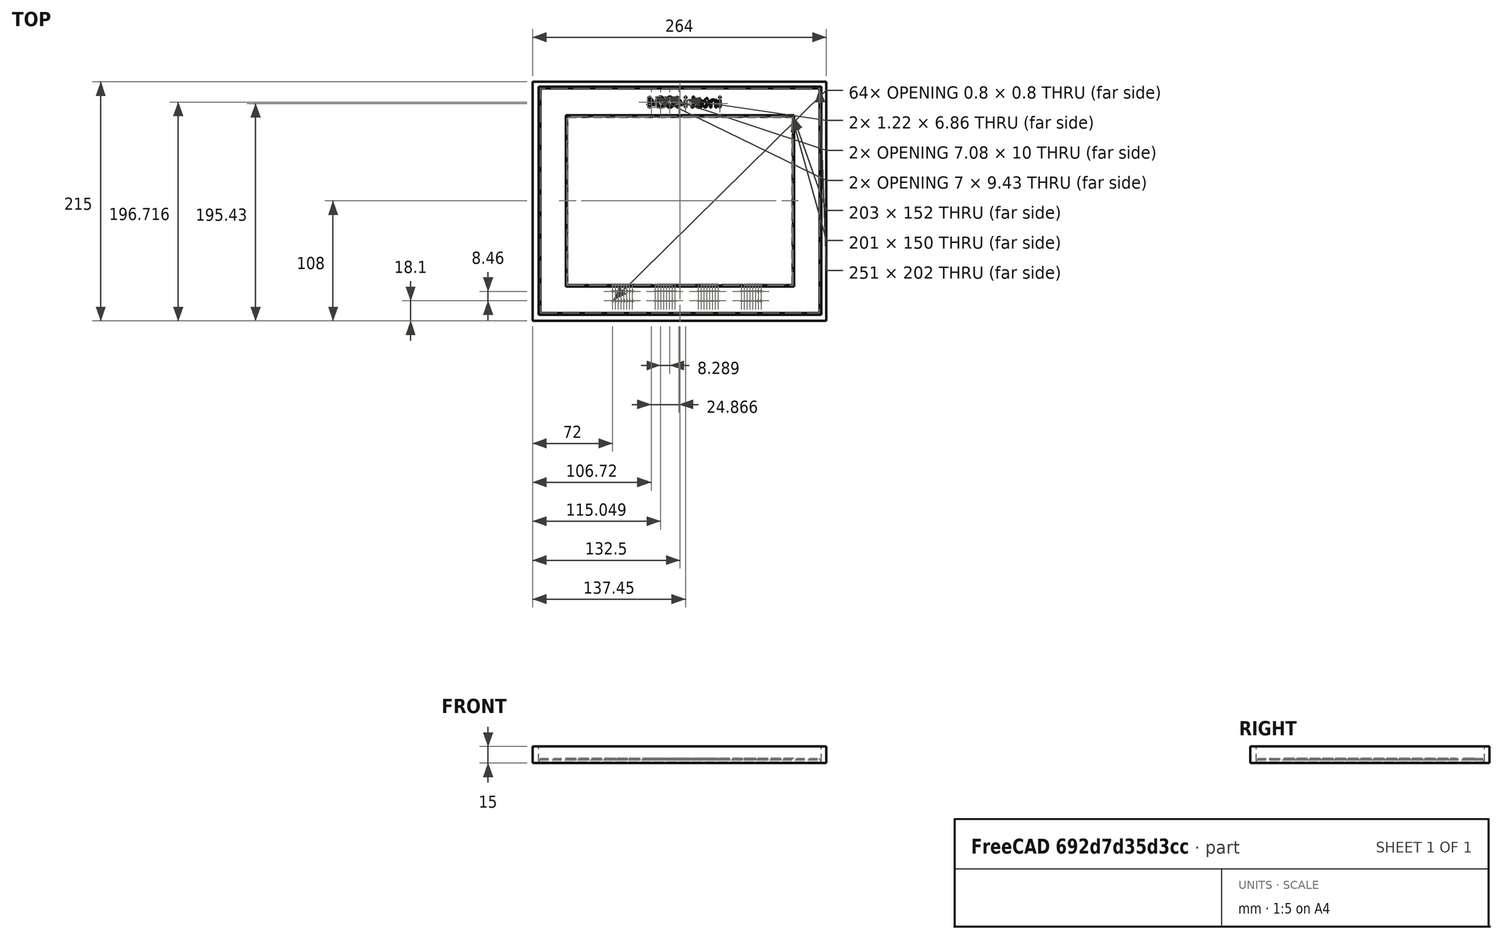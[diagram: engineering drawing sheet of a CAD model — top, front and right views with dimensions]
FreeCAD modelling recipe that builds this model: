
FCSTD DOCUMENT  (FreeCAD 0.18R4 (GitTag))
Label: Frame
License: All rights reserved
LicenseURL: http://en.wikipedia.org/wiki/All_rights_reserved
objects: Part::Box×9, Part::Cut×5, Part::Feature×5, Part::MultiFuse×2, App::DocumentObjectGroup×1, Part::Part2DObjectPython×1, Part::Extrusion×1
note: 23 computed .brp shape members not serialized (recipe doc carries the construction recipe); baked Part::Feature solids carry a one-line shape summary decoded from their .brp

FEATURE [Part::Box] Box  label="Picture"
  AttacherType = Attacher::AttachEngine3D
  Height = 0.1
  Length = 203
  Placement = pos=(31,32,4.14) rot=(0,0,1;0rad)
  Width = 152
FEATURE [Part::Box] Box002  label="Glass"
  AttacherType = Attacher::AttachEngine3D
  Height = 2.12
  Length = 253
  Placement = pos=(6,6,1) rot=(0,0,1;0rad)
  Width = 204
FEATURE [Part::Box] Box003  label="FrameOuter"
  AttacherType = Attacher::AttachEngine3D
  Height = 15
  Length = 264
  Width = 215
FEATURE [Part::Box] Box004  label="FrameCutOut1"
  AttacherType = Attacher::AttachEngine3D
  Height = 16
  Length = 254
  Placement = pos=(5.5,5.5,1) rot=(0,0,1;0rad)
  Width = 205
FEATURE [Part::Box] Box005  label="FrameCutOut2"
  AttacherType = Attacher::AttachEngine3D
  Height = 1
  Length = 251
  Placement = pos=(7,7,0) rot=(0,0,1;0rad)
  Width = 202
FEATURE [Part::Cut] Cut
  Base = -> Box003
  Tool = -> Box004
FEATURE [Part::Cut] Cut001  label="Frame (Model)"
  Base = -> Cut
  Tool = -> Box005
FEATURE [App::DocumentObjectGroup] Group  label="Frame001"
  Group = -> [Cut001,Box002]
FEATURE [Part::Box] Box007  label="InsertMain"
  AttacherType = Attacher::AttachEngine3D
  Height = 1
  Length = 251
  Placement = pos=(7,7,0) rot=(0,0,1;0rad)
  Width = 202
FEATURE [Part::Box] Box008  label="InsertCutOut"
  AttacherType = Attacher::AttachEngine3D
  Height = 1
  Length = 201
  Placement = pos=(32,33,0) rot=(0,0,1;0rad)
  Width = 150
FEATURE [Part::Cut] Cut002  label="Insert001"
  Base = -> Box007
  Placement = pos=(0,0,3.13) rot=(0,0,1;0rad)
  Tool = -> Box008
FEATURE [Part::Box] Box009  label="InsertGuideCutout"
  AttacherType = Attacher::AttachEngine3D
  Height = 0.5
  Length = 203
  Placement = pos=(31,32,4.14) rot=(0,0,1;0rad)
  Width = 152
FEATURE [Part::Box] Box010  label="InsertGuideMain"
  AttacherType = Attacher::AttachEngine3D
  Height = 0.5
  Length = 205
  Placement = pos=(30,31,4.14) rot=(0,0,1;0rad)
  Width = 154
FEATURE [Part::Cut] Cut003  label="InsertGuide"
  Base = -> Box010
  Tool = -> Box009
FEATURE [Part::Part2DObjectPython] ShapeString  # Draft 2D object (typed FeaturePython)
  FontFile = <userpath>/Desktop/Intel Clear Arabic Regular.ttf
  Size = 12
  String = intel i4004
  Tracking = 0
FEATURE [Part::Extrusion] Extrude  label="intel i4004"
  Base = -> ShapeString
  Dir = (0,0,1)
  DirMode = 2
  FaceMakerClass = Part::FaceMakerBullseye
  LengthFwd = 10
  LengthRev = 0
  Placement = pos=(170,192,5) rot=(0,1,0;3.14159rad)
  Solid = false
  Symmetric = false
FEATURE [Part::Feature] i4004_FatLeg005_solid  label="i4004_FatLeg001 (Solid)"
  shape: bbox 21.53 x 9.26 x 7.69 mm, 2052 faces (baked)
FEATURE [Part::Feature] i4004_FatLeg008_solid  label="i4004_FatLeg004 (Solid)"
  shape: bbox 21.53 x 9.26 x 7.69 mm, 2052 faces (baked)
FEATURE [Part::Feature] i4004_FatLeg006_solid  label="i4004_FatLeg002 (Solid)"
  shape: bbox 21.53 x 9.26 x 7.69 mm, 2052 faces (baked)
FEATURE [Part::Feature] i4004_FatLeg007_solid  label="i4004_FatLeg003 (Solid)"
  shape: bbox 21.53 x 9.26 x 7.69 mm, 2052 faces (baked)
FEATURE [Part::MultiFuse] Fusion
  Shapes = -> [i4004_FatLeg005_solid,i4004_FatLeg008_solid,i4004_FatLeg006_solid,i4004_FatLeg007_solid,Extrude]
FEATURE [Part::Cut] Cut004
  Base = -> Cut002
  Tool = -> Fusion
FEATURE [Part::MultiFuse] Fusion001  label="FrameInsert"
  Shapes = -> [Cut003,Cut004]
FEATURE [Part::Feature] Cut001_solid  label="Frame (Solid)"
  shape: bbox 264 x 215 x 15 mm, 15 faces (baked)
